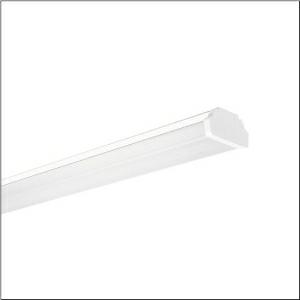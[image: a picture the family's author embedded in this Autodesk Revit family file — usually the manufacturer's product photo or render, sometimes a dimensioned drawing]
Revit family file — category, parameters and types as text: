
# Revit family: dus_r__31_gen_2_53bd812dv4a5c2_6be2
name_source: partatom
category: Lighting Fixtures
units: mm (PartAtom-declared; Revit-internal decimal feet)

## family parameters
Cut with Voids When Loaded = No
Host = Face
Light Source = No
Part Type = Normal
Room Calculation Point = No
Round Connector Dimension = Use Diameter
Shared = No

## types (1)
- --- (1 x LED, 10860 lm, 61.4 W, 4000K)
    Apparent Load = 61 VA
    CIE Flux Codes = 47 80 95 93 100
    Color Rendering = 80
    Color Temperature = 4000K
    Default Elevation = 1800 mm
    Description = DUS® 31 Gen.2, luminaire insert, of sheet steel, coil coated, white, length: 1.535mm, width: 81mm, height: 90mm, 5x system unit, system units: 307mm, LED rated luminous flux: 10.860lm, light colour: 840, control gear: DALI 2, control gear: ECG DALI, with plug, 5-pole, with phase selection, mains connection: 220..240V, AC, 50/60Hz, rated input power: 61W, through-wiring accessed according to module size, primary optical cover: cover, of PMMA, light emission: direct distribution, primary light characteristic: symmetric, protection rating (complete): IP20, protection rating (LED compartment): IP50, insulation class (complete): insulation class I (protective earthing), certification: CE, ENEC, VDE, UKCA, impact resistance: IK03, permissible ambient temperature for indoor applications: -25..+35°C, corresponds to IFS (International Featured Standards) requirements for safety and quality in the food industry, reducing of maximum allowable ambient temperature of 5°C with ceiling mounting, packaging unit: 1 piece
    Height = 95 mm
    Lamp = 1 x LED
    Lamp Light Flux = 10860 lm
    Lamp Power = 61.4 W
    Lamp count = 1
    Length = 1535 mm
    Luminous efficacy = 177 lm/W
    Manufacturer = Siteco
    ModVariant = No
    Model = 53BD812DV4A5C2
    Mounting Place = Ceiling
    Mounting Type = Pendant
    Number of Poles = 1
    OnlyDefault = Yes
    Power Factor = 1
    Product Name = DUS® 31 Gen.2
    Product group = luminaire insert
    ProductGroupID = 902
    Protection Class = Protection class I
    Protection Degree = IP 20
    RLX_Detail_Level = 1
    RLX_Emergency_Light_Flux = 0 lm
    RLX_Emergency_Type = 0
    RLX_Emergency_Type_DB = No
    RlxData = <blob elided: 32081 chars, md5=97b10ec1>
    Socket = socket
    Standby Power = 0 W
    System Light Flux = 10860 lm
    System Power = 61 W
    Type Comments = factory setting: luminous flux: 100 % | dim-lin: 254 | 418 mA
    Type Image = l_1319596.jpg
    URL = http://relux.com
    VarID = @adj_042438
    Voltage = 0 V
    Weight = 0.00 kg
    Width = 81 mm

## geometry (parser evidence)
native form markers: Blend x4, Sweep x13
no freeform markers — native parametric forms only
